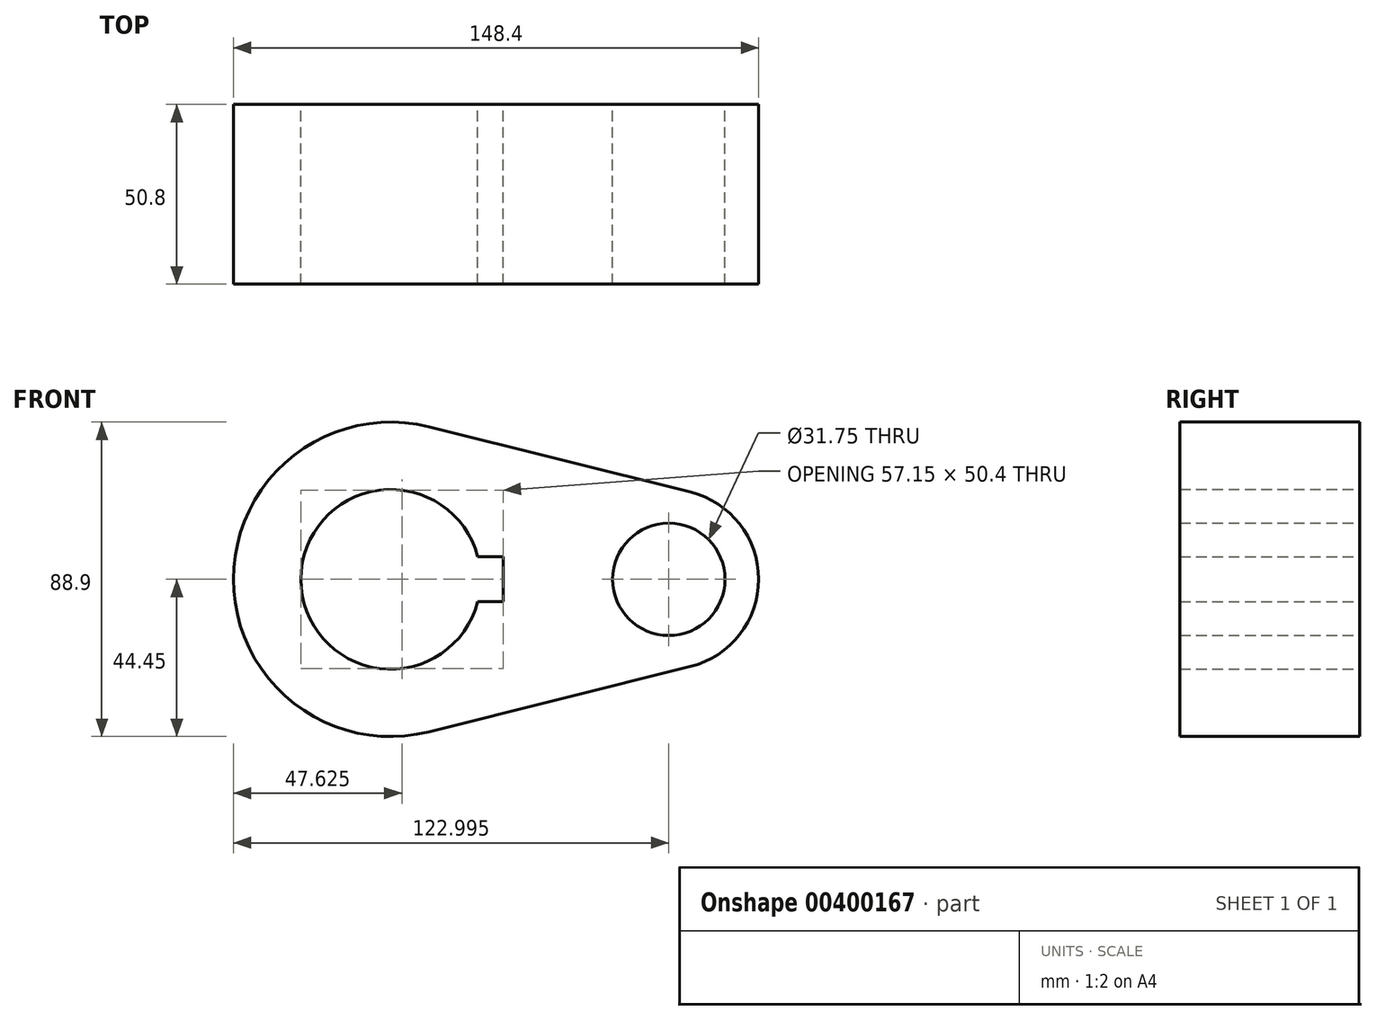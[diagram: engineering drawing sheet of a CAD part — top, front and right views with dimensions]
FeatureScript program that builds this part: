
annotation { "Feature Type Name" : "Feature", "Feature Type Description" : "" }
export const myFeature = defineFeature(function(context is Context, id is Id, definition is map)
    precondition{}
    {
        {
            var Q0;
            Q0=qCreatedBy(makeId("Front.planeOp"),FACE);
            var sketch = newSketch(context, id + "F0", { "sketchPlane" : qUnion([Q0])});
            skCircle(sketch, "E0", {"center": v(0, 0) * mm, "radius": 44.45 * mm});
            skCircle(sketch, "E1", {"center": v(78.55, 0) * mm, "radius": 25.4 * mm});
            skLineSegment(sketch, "E2", {"start": v(10.78, 43.12) * mm, "end": v(84.7, 24.64) * mm});
            skLineSegment(sketch, "E3", {"start": v(10.78, -43.12) * mm, "end": v(84.7, -24.64) * mm});
            skCircle(sketch, "E4", {"center": v(78.55, 0) * mm, "radius": 15.88 * mm});
            skCircle(sketch, "E5", {"center": v(0, 0) * mm, "radius": 25.4 * mm});
            skLineSegment(sketch, "E6.bottom", {"start": v(31.75, 6.35) * mm, "end": v(-31.75, 6.35) * mm});
            skLineSegment(sketch, "E6.top", {"start": v(31.75, -6.35) * mm, "end": v(-31.75, -6.35) * mm});
            skLineSegment(sketch, "E6.left", {"start": v(31.75, 6.35) * mm, "end": v(31.75, -6.35) * mm});
            skLineSegment(sketch, "E6.right", {"start": v(-31.75, 6.35) * mm, "end": v(-31.75, -6.35) * mm});
            skSolve(sketch);
        }
        {
            var Q0;
            Q0 = qSketchRegion(id + "F0", true);
            var Q1;
            {var subQ5=sQuery(id+"F0.wireOp",EDGE,"E6.right");Q1=makeQuery(id+"F0.imprint","IMPRINT",FACE,{"disambiguationData":[TD([[makeQuery(id+"F0.imprint","IMPRINT",EDGE,{"derivedFrom":subQ5}),1.0]])]});}
            extrude(context, id + "F1", {"entities" : qUnion([Q0, Q1]), "depth" : 50.8 * mm});
        }
    });
